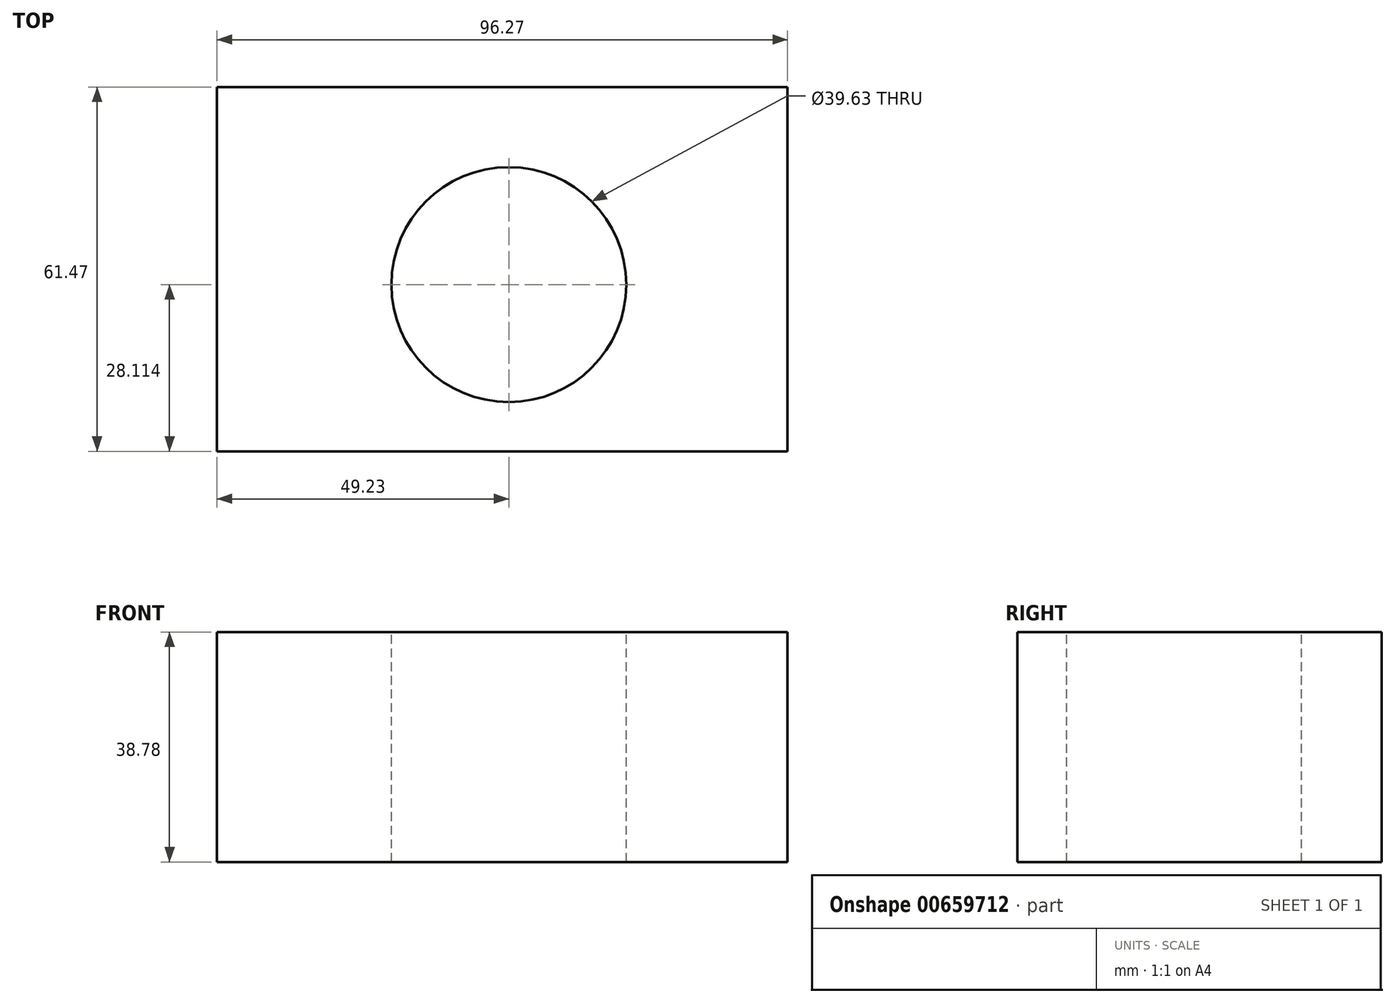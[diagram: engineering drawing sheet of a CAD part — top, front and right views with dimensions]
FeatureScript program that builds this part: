
annotation { "Feature Type Name" : "Feature", "Feature Type Description" : "" }
export const myFeature = defineFeature(function(context is Context, id is Id, definition is map)
    precondition{}
    {
        {
            var Q0;
            Q0=qCreatedBy(makeId("Front.planeOp"),FACE);
            var sketch = newSketch(context, id + "F0", { "sketchPlane" : qUnion([Q0])});
            skLineSegment(sketch, "E0", {"start": v(0, 0) * mm, "end": v(96.27, 0) * mm});
            skLineSegment(sketch, "E1", {"start": v(96.27, 0) * mm, "end": v(96.27, 38.78) * mm});
            skLineSegment(sketch, "E2", {"start": v(96.27, 38.78) * mm, "end": v(0, 38.78) * mm});
            skLineSegment(sketch, "E3", {"start": v(0, 38.78) * mm, "end": v(0, 0) * mm});
            skSolve(sketch);
        }
        {
            var Q0;
            Q0 = qSketchRegion(id + "F0", true);
            extrude(context, id + "F1", {"entities" : qUnion([Q0]), "depth" : 61.47 * mm, "offsetDistance" : 25.4 * mm});
        }
        {
            var Q0;
            Q0=makeQuery(id+"F1.opExtrude","SWEPT_FACE",FACE,{"disambiguationData":[OSD([sQuery(id+"F0.wireOp",EDGE,"E2")])]});
            var sketch = newSketch(context, id + "F2", { "sketchPlane" : qUnion([Q0])});
            skCircle(sketch, "E4", {"center": v(49.23, -33.36) * mm, "radius": 19.81 * mm});
            skSolve(sketch);
        }
        {
            var Q0;
            Q0 = qSketchRegion(id + "F2", true);
            extrude(context, id + "F3", {"entities" : qUnion([Q0]), "operationType" : NewBodyOperationType.REMOVE, "endBound" : BoundingType.THROUGH_ALL, "oppositeDirection" : true, "depth" : 25.4 * mm, "offsetDistance" : 25.4 * mm});
        }
    });
